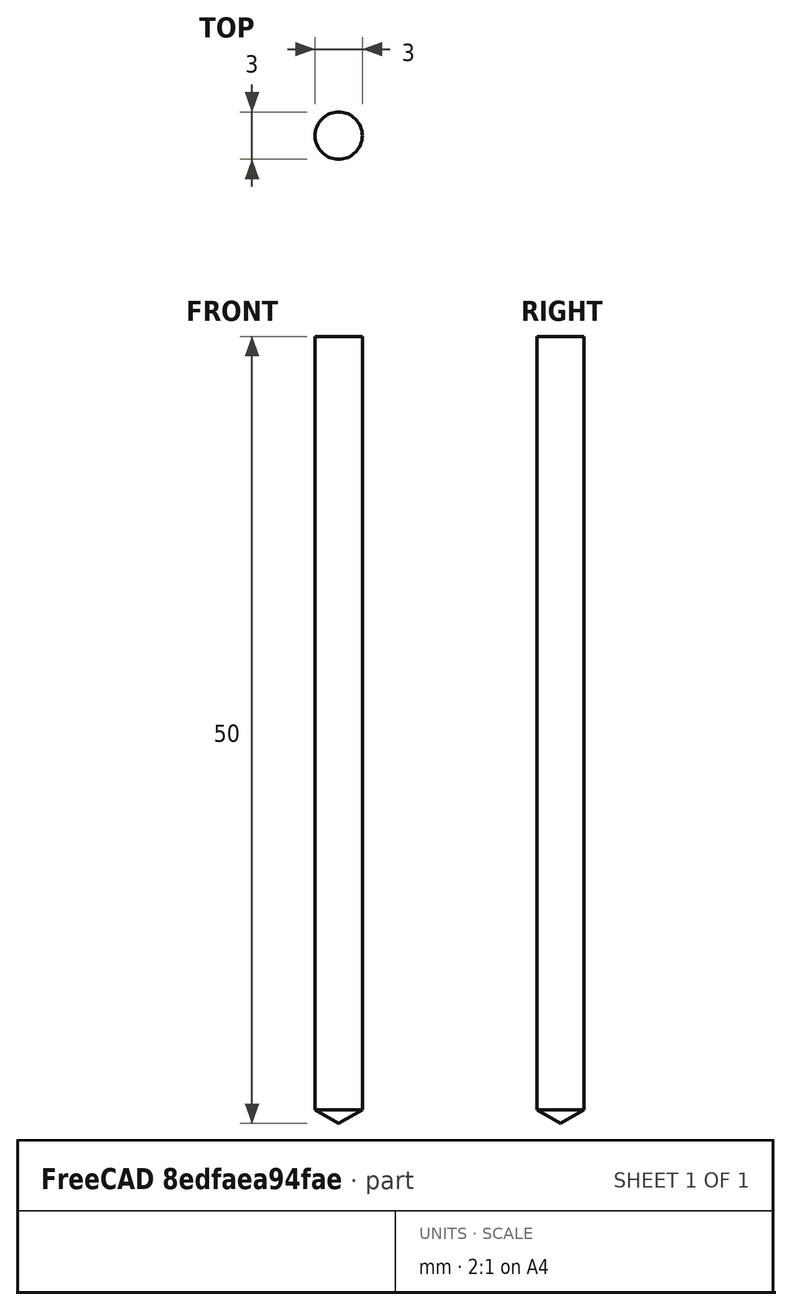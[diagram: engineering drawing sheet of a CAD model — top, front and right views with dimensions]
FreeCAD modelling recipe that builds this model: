
FCSTD DOCUMENT  (FreeCAD 0.19R24049 (Git))
Label: drill
License: All rights reserved
LicenseURL: http://en.wikipedia.org/wiki/All_rights_reserved
objects: Sketcher::SketchObject×1, PartDesign::Revolution×1, App::FeaturePython×1, PartDesign::Body×1
note: 4 computed .brp shape members not serialized (recipe doc carries the construction recipe); baked Part::Feature solids carry a one-line shape summary decoded from their .brp

FEATURE [Sketcher::SketchObject] Sketch
  FullyConstrained = true
  MapMode = 5
  Placement = pos=(0,0,0) rot=(1,0,0;1.5708rad)
  Support = -> [XZ_Plane]
  expr: Constraints[15] = <<Attributes>>.Length
  expr: Constraints[13] = <<Attributes>>.TipAngle
  expr: Constraints[14] = <<Attributes>>.Diameter
  sketch-geometry (7):
    g0: LineSegment StartX=0 StartY=50 StartZ=0 EndX=0 EndY=0 EndZ=0
    g1: LineSegment StartX=0 StartY=0 StartZ=0 EndX=1.5 EndY=0.883568 EndZ=0
    g2: LineSegment StartX=1.5 StartY=0.883568 StartZ=0 EndX=1.5 EndY=50 EndZ=0
    g3: LineSegment StartX=1.5 StartY=50 StartZ=0 EndX=0 EndY=50 EndZ=0
    g4: LineSegment StartX=1.5 StartY=0.883568 StartZ=0 EndX=-1.5 EndY=0.883568 EndZ=0
    g5: LineSegment StartX=-1.5 StartY=0.883568 StartZ=0 EndX=0 EndY=0 EndZ=0
    g6: LineSegment StartX=0 StartY=0 StartZ=0 EndX=1.5 EndY=0.883568 EndZ=0
  constraints (17):
    c: Vertical(g0)
    c: Coincident(g0,g1)
    c: Coincident(g1,g2)
    c: Vertical(g2)
    c: Coincident(g2,g3)
    c: Horizontal(g3)
    c: Coincident(g0,g3)
    c: Coincident(g4,g5)
    c: Coincident(g5,g6)
    c: Coincident(g6,g4)
    c: Coincident(g1,g4)
    c: Coincident(g5,g0)
    c: Symmetric(g4,g1,g0)
    c: Angle(g1,g5) = 2.07694
    c: DistanceX(g4,g4) = 3
    c: DistanceY(g0,g0) = 50
    c: Coincident(g0,g-1)
FEATURE [PartDesign::Revolution] Revolution
  AllowMultiFace = false
  Angle = 360
  Axis = (0,-2e-16,1)
  Base = (0,0,0)
  Placement = pos=(0,0,0) rot=(1,0,0;1.5708rad)
  Profile = -> Sketch
  ReferenceAxis = -> Sketch [V_Axis]
  Reversed = true
FEATURE [App::FeaturePython] PropertyBag  label="Attributes"  # WARN: FeaturePython — macro-defined, semantics opaque (R4)
  Chipload = 0
  CustomPropertyGroups = Attributes | Shape
  Diameter = 3
  Flutes = 0
  Length = 50
  Material = 0
  TipAngle = 119
FEATURE [PartDesign::Body] Body  label="Drill"
  Group = -> [Sketch,Revolution,PropertyBag]
  Origin = -> Origin
  Tip = -> Revolution
